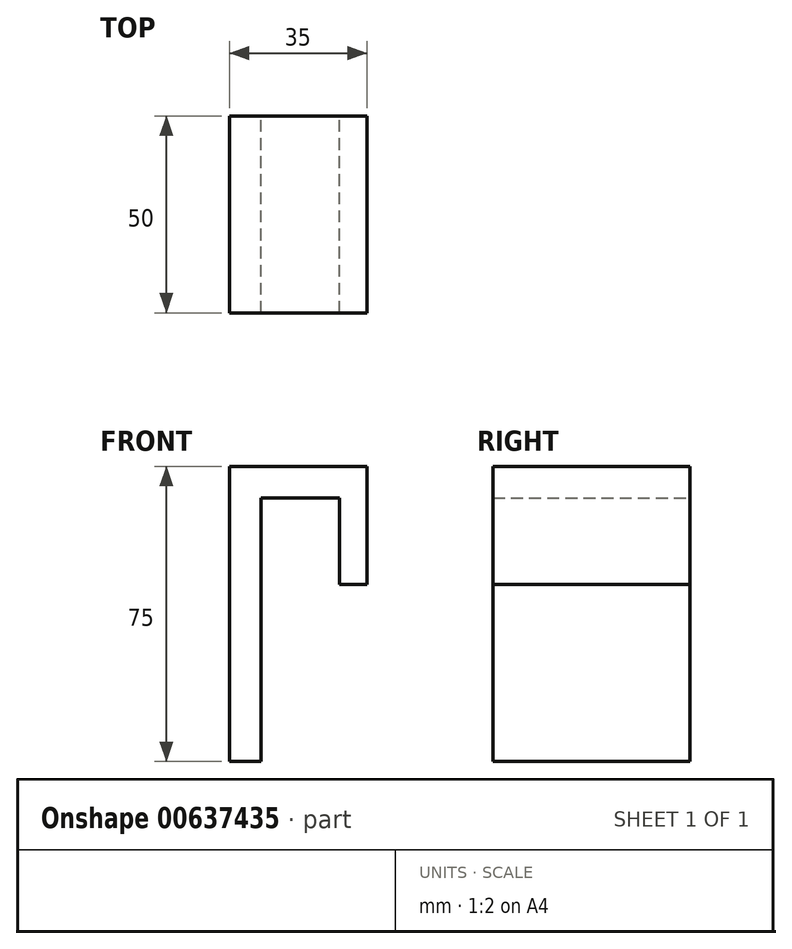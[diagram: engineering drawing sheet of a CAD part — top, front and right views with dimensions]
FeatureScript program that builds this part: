
annotation { "Feature Type Name" : "Feature", "Feature Type Description" : "" }
export const myFeature = defineFeature(function(context is Context, id is Id, definition is map)
    precondition{}
    {
        {
            var Q0;
            Q0=qCreatedBy(makeId("Front.planeOp"),FACE);
            var sketch = newSketch(context, id + "F0", { "sketchPlane" : qUnion([Q0])});
            skLineSegment(sketch, "E0.bottom", {"start": v(-18.37, 22.95) * mm, "end": v(1.63, 22.95) * mm});
            skLineSegment(sketch, "E0.top", {"start": v(-26.37, 30.95) * mm, "end": v(8.63, 30.95) * mm});
            skLineSegment(sketch, "E0.left", {"start": v(-26.37, 30.95) * mm, "end": v(-26.37, 22.95) * mm});
            skLineSegment(sketch, "E0.right", {"start": v(8.63, 30.95) * mm, "end": v(8.63, 22.95) * mm});
            skLineSegment(sketch, "E1.bottom", {"start": v(8.63, 30.95) * mm, "end": v(1.63, 30.95) * mm});
            skLineSegment(sketch, "E1.top", {"start": v(8.63, 0.95) * mm, "end": v(1.63, 0.95) * mm});
            skLineSegment(sketch, "E1.left", {"start": v(8.63, 30.95) * mm, "end": v(8.63, 0.95) * mm});
            skLineSegment(sketch, "E1.right", {"start": v(1.63, 22.95) * mm, "end": v(1.63, 0.95) * mm});
            skLineSegment(sketch, "E2.bottom", {"start": v(-26.37, 30.95) * mm, "end": v(-18.37, 30.95) * mm});
            skLineSegment(sketch, "E2.top", {"start": v(-26.37, -44.05) * mm, "end": v(-18.37, -44.05) * mm});
            skLineSegment(sketch, "E2.left", {"start": v(-26.37, 30.95) * mm, "end": v(-26.37, -44.05) * mm});
            skLineSegment(sketch, "E2.right", {"start": v(-18.37, 22.95) * mm, "end": v(-18.37, -44.05) * mm});
            skSolve(sketch);
        }
        {
            var Q0;
            Q0 = qSketchRegion(id + "F0", true);
            extrude(context, id + "F1", {"entities" : qUnion([Q0]), "depth" : 50 * mm, "offsetDistance" : 25 * mm});
        }
    });
